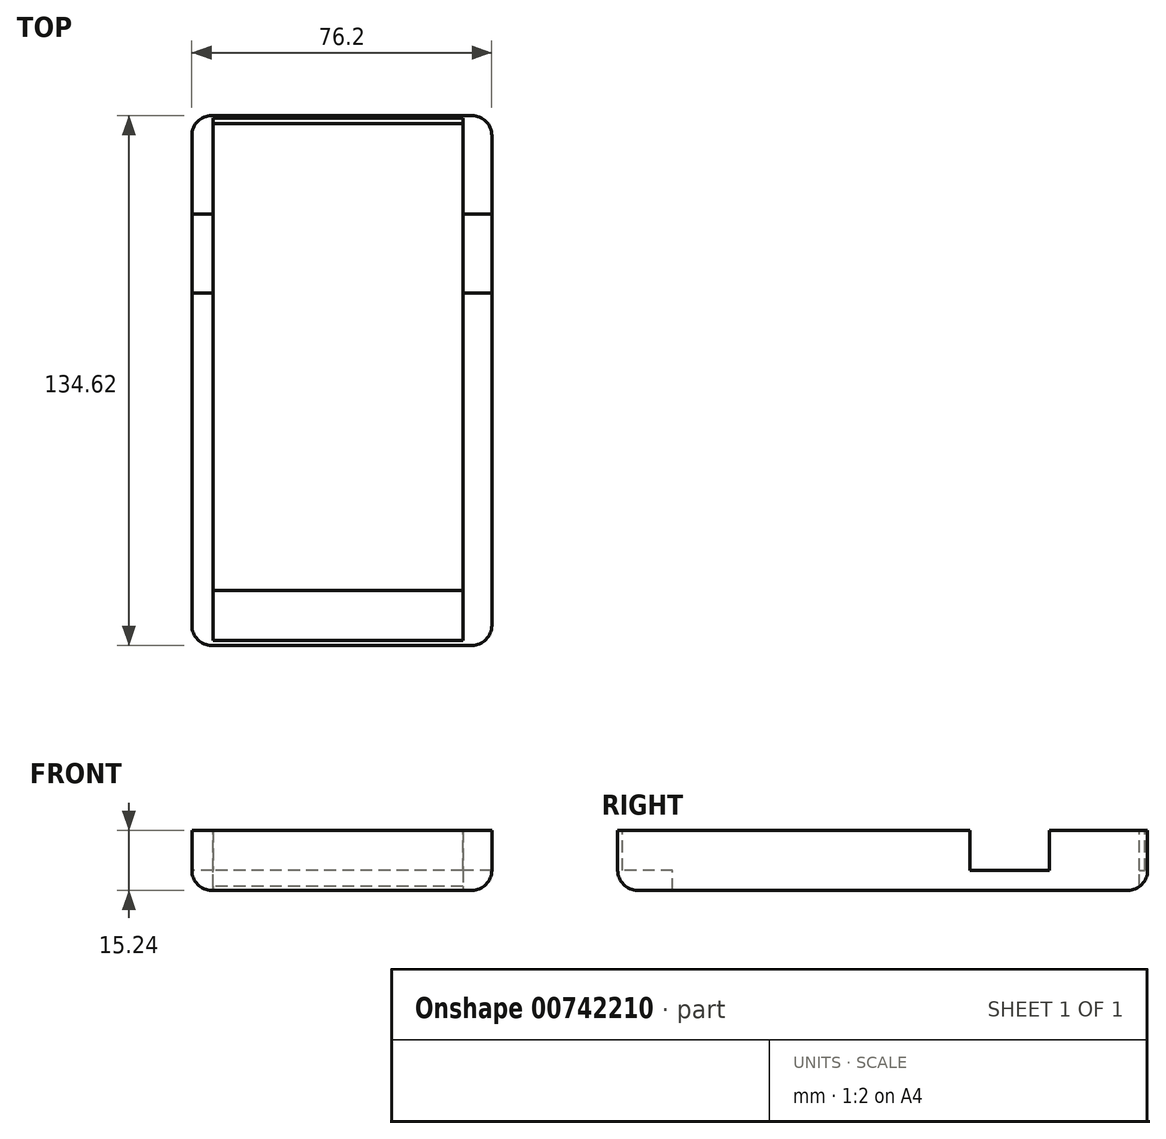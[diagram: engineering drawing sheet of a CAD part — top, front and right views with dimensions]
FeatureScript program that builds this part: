
annotation { "Feature Type Name" : "Feature", "Feature Type Description" : "" }
export const myFeature = defineFeature(function(context is Context, id is Id, definition is map)
    precondition{}
    {
        {
            var Q0;
            Q0=qCreatedBy(makeId("Top.planeOp"),FACE);
            var sketch = newSketch(context, id + "F0", { "sketchPlane" : qUnion([Q0])});
            skLineSegment(sketch, "E0.bottom", {"start": v(-32.63, 82.97) * mm, "end": v(43.57, 82.97) * mm});
            skLineSegment(sketch, "E0.top", {"start": v(-32.63, -51.65) * mm, "end": v(43.57, -51.65) * mm});
            skLineSegment(sketch, "E0.left", {"start": v(-32.63, 82.97) * mm, "end": v(-32.63, -51.65) * mm});
            skLineSegment(sketch, "E0.right", {"start": v(43.57, 82.97) * mm, "end": v(43.57, -51.65) * mm});
            skSolve(sketch);
        }
        {
            var Q0;
            Q0=makeQuery(id+"F0.imprint","IMPRINT",FACE,{"disambiguationData":[TD([[makeQuery(id+"F0.imprint","IMPRINT",EDGE,{"derivedFrom":sQuery(id+"F0.wireOp",EDGE,"E0.bottom")}),-1.0]])]});
            extrude(context, id + "F1", {"entities" : qUnion([Q0]), "depth" : 15.24 * mm, "offsetDistance" : 25.4 * mm});
        }
        {
            var Q0;
            Q0=makeQuery(id+"F0.imprint","IMPRINT",FACE,{"disambiguationData":[TD([[makeQuery(id+"F0.imprint","IMPRINT",EDGE,{"derivedFrom":sQuery(id+"F0.wireOp",EDGE,"E0.bottom")}),-1.0]])]});
            var sketch = newSketch(context, id + "F2", { "sketchPlane" : qUnion([Q0])});
            skLineSegment(sketch, "E1.bottom", {"start": v(-27.3, -37.69) * mm, "end": v(36.2, -37.69) * mm});
            skLineSegment(sketch, "E1.top", {"start": v(-27.3, 80.92) * mm, "end": v(36.2, 80.92) * mm});
            skLineSegment(sketch, "E1.left", {"start": v(-27.3, -37.69) * mm, "end": v(-27.3, 80.92) * mm});
            skLineSegment(sketch, "E1.right", {"start": v(36.2, -37.69) * mm, "end": v(36.2, 80.92) * mm});
            skLineSegment(sketch, "E2.bottom", {"start": v(36.2, 80.92) * mm, "end": v(-27.3, 80.92) * mm});
            skLineSegment(sketch, "E2.top", {"start": v(36.2, 81.81) * mm, "end": v(-27.3, 81.81) * mm});
            skLineSegment(sketch, "E2.left", {"start": v(36.2, 80.92) * mm, "end": v(36.2, 81.81) * mm});
            skLineSegment(sketch, "E2.right", {"start": v(-27.3, 80.92) * mm, "end": v(-27.3, 81.81) * mm});
            skSolve(sketch);
        }
        {
            var Q0;
            Q0=makeQuery(id+"F2.imprint","IMPRINT",FACE,{"disambiguationData":[TD([[makeQuery(id+"F2.imprint","IMPRINT",EDGE,{"derivedFrom":sQuery(id+"F2.wireOp",EDGE,"E1.bottom")}),1.0]])]});
            extrude(context, id + "F3", {"entities" : qUnion([Q0]), "operationType" : NewBodyOperationType.REMOVE, "endBound" : BoundingType.THROUGH_ALL, "depth" : 25.4 * mm, "offsetDistance" : 25.4 * mm});
        }
        {
            var Q0;
            Q0=makeQuery(id+"F1.opExtrude","CAP_FACE",FACE,{"disambiguationData":[OSD([sQuery(id+"F0.wireOp",EDGE,"E0.bottom"),sQuery(id+"F0.wireOp",EDGE,"E0.top"),sQuery(id+"F0.wireOp",EDGE,"E0.left"),sQuery(id+"F0.wireOp",EDGE,"E0.right")])],"isStart":false});
            var sketch = newSketch(context, id + "F4", { "sketchPlane" : qUnion([Q0])});
            skLineSegment(sketch, "E3.bottom", {"start": v(36.2, -37.69) * mm, "end": v(-27.3, -37.69) * mm});
            skLineSegment(sketch, "E3.top", {"start": v(36.2, -50.38) * mm, "end": v(-27.3, -50.38) * mm});
            skLineSegment(sketch, "E3.left", {"start": v(36.2, -37.69) * mm, "end": v(36.2, -50.38) * mm});
            skLineSegment(sketch, "E3.right", {"start": v(-27.3, -37.69) * mm, "end": v(-27.3, -50.38) * mm});
            skSolve(sketch);
        }
        {
            var Q0;
            Q0=makeQuery(id+"F4.imprint","IMPRINT",FACE,{"disambiguationData":[TD([[makeQuery(id+"F4.imprint","IMPRINT",EDGE,{"derivedFrom":sQuery(id+"F4.wireOp",EDGE,"E3.bottom")}),1.0]])]});
            extrude(context, id + "F5", {"entities" : qUnion([Q0]), "operationType" : NewBodyOperationType.REMOVE, "oppositeDirection" : true, "depth" : 10.16 * mm, "offsetDistance" : 25.4 * mm});
        }
        {
            var Q0;
            Q0=makeQuery(id+"F4.imprint","IMPRINT",FACE,{"disambiguationData":[TD([[makeQuery(id+"F4.imprint","IMPRINT",EDGE,{"derivedFrom":sQuery(id+"F4.wireOp",EDGE,"E3.top")}),1.0]])]});
            var sketch = newSketch(context, id + "F6", { "sketchPlane" : qUnion([Q0])});
            skLineSegment(sketch, "E4.bottom", {"start": v(36.2, 80.91) * mm, "end": v(-27.3, 80.91) * mm});
            skLineSegment(sketch, "E4.top", {"start": v(36.2, 82.33) * mm, "end": v(-27.3, 82.33) * mm});
            skLineSegment(sketch, "E4.left", {"start": v(36.2, 80.91) * mm, "end": v(36.2, 82.33) * mm});
            skLineSegment(sketch, "E4.right", {"start": v(-27.3, 80.91) * mm, "end": v(-27.3, 82.33) * mm});
            skSolve(sketch);
        }
        {
            var Q0;
            {var subQ1=sQuery(id+"F6.wireOp",EDGE,"E4.top");Q0=makeQuery(id+"F6.imprint","IMPRINT",FACE,{"disambiguationData":[TD([[makeQuery(id+"F6.imprint","IMPRINT",EDGE,{"derivedFrom":subQ1}),1.0]])]});}
            extrude(context, id + "F7", {"entities" : qUnion([Q0]), "operationType" : NewBodyOperationType.REMOVE, "oppositeDirection" : true, "depth" : 10.16 * mm, "offsetDistance" : 25.4 * mm});
        }
        {
            var Q0;
            Q0=makeQuery(id+"F1.opExtrude","CAP_EDGE",EDGE,{"disambiguationData":[OSD([sQuery(id+"F0.wireOp",EDGE,"E0.right")])],"isStart":true});
            var Q1;
            Q1=makeQuery(id+"F1.opExtrude","CAP_EDGE",EDGE,{"disambiguationData":[OSD([sQuery(id+"F0.wireOp",EDGE,"E0.bottom")])],"isStart":true});
            var Q2;
            Q2=makeQuery(id+"F1.opExtrude","CAP_EDGE",EDGE,{"disambiguationData":[OSD([sQuery(id+"F0.wireOp",EDGE,"E0.left")])],"isStart":true});
            var Q3;
            Q3=makeQuery(id+"F1.opExtrude","CAP_EDGE",EDGE,{"disambiguationData":[OSD([sQuery(id+"F0.wireOp",EDGE,"E0.top")])],"isStart":true});
            fillet(context, id + "F8", {"entities" : qUnion([Q0, Q1, Q2, Q3]), "radius" : 5.08 * mm, "tangentPropagation" : true, "allowEdgeOverflow" : false});
        }
        {
            var Q0;
            {var subQ0=sQuery(id+"F0.wireOp",EDGE,"E0.left");Q0=makeQuery(id+"F8.opFillet","BLEND_EDGE",EDGE,{"blendedFrom":[makeQuery(id+"F1.opExtrude","CAP_EDGE",EDGE,{"disambiguationData":[OSD([subQ0])],"isStart":true}),makeQuery(id+"F1.opExtrude","SWEPT_FACE",FACE,{"disambiguationData":[OSD([subQ0])]})],"blendedInto":[makeQuery(id+"F1.opExtrude","SWEPT_FACE",FACE,{"disambiguationData":[OSD([subQ0])]})]});}
            var Q1;
            Q1=makeQuery(id+"F8.opFillet","BLEND_EDGE",EDGE,{"blendedFrom":[makeQuery(id+"F1.opExtrude","CAP_EDGE",EDGE,{"disambiguationData":[OSD([sQuery(id+"F0.wireOp",EDGE,"E0.top")])],"isStart":true}),makeQuery(id+"F1.opExtrude","CAP_EDGE",EDGE,{"disambiguationData":[OSD([sQuery(id+"F0.wireOp",EDGE,"E0.left")])],"isStart":true})],"blendedInto":[]});
            var Q2;
            Q2=makeQuery(id+"F8.opFillet","BLEND_EDGE",EDGE,{"blendedFrom":[makeQuery(id+"F1.opExtrude","CAP_EDGE",EDGE,{"disambiguationData":[OSD([sQuery(id+"F0.wireOp",EDGE,"E0.bottom")])],"isStart":true}),makeQuery(id+"F1.opExtrude","CAP_EDGE",EDGE,{"disambiguationData":[OSD([sQuery(id+"F0.wireOp",EDGE,"E0.left")])],"isStart":true})],"blendedInto":[]});
            var Q3;
            Q3=makeQuery(id+"F8.opFillet","BLEND_EDGE",EDGE,{"blendedFrom":[makeQuery(id+"F1.opExtrude","CAP_EDGE",EDGE,{"disambiguationData":[OSD([sQuery(id+"F0.wireOp",EDGE,"E0.bottom")])],"isStart":true}),makeQuery(id+"F1.opExtrude","CAP_EDGE",EDGE,{"disambiguationData":[OSD([sQuery(id+"F0.wireOp",EDGE,"E0.right")])],"isStart":true})],"blendedInto":[]});
            var Q4;
            Q4=makeQuery(id+"F8.opFillet","BLEND_EDGE",EDGE,{"blendedFrom":[makeQuery(id+"F1.opExtrude","CAP_EDGE",EDGE,{"disambiguationData":[OSD([sQuery(id+"F0.wireOp",EDGE,"E0.top")])],"isStart":true}),makeQuery(id+"F1.opExtrude","CAP_EDGE",EDGE,{"disambiguationData":[OSD([sQuery(id+"F0.wireOp",EDGE,"E0.right")])],"isStart":true})],"blendedInto":[]});
            fillet(context, id + "F9", {"entities" : qUnion([Q0, Q1, Q2, Q3, Q4]), "radius" : 5.08 * mm, "tangentPropagation" : true, "allowEdgeOverflow" : false});
        }
        {
            var Q0;
            Q0=makeQuery(id+"F1.opExtrude","SWEPT_FACE",FACE,{"disambiguationData":[OSD([sQuery(id+"F0.wireOp",EDGE,"E0.left")])]});
            var sketch = newSketch(context, id + "F10", { "sketchPlane" : qUnion([Q0])});
            skLineSegment(sketch, "E5", {"start": v(-83.37, 10.16) * mm, "end": v(-57.97, 10.16) * mm});
            skPoint(sketch, "E5.startSnap0", {"position": v(-77.9, 10.16) * mm});
            skLineSegment(sketch, "E6", {"start": v(51.05, 10.16) * mm, "end": v(-37.85, 10.16) * mm});
            skPoint(sketch, "E6.startSnap0", {"position": v(46.57, 10.16) * mm});
            skLineSegment(sketch, "E7.bottom", {"start": v(-37.85, 15.24) * mm, "end": v(-57.97, 15.24) * mm});
            skLineSegment(sketch, "E7.top", {"start": v(-37.85, 5.08) * mm, "end": v(-57.97, 5.08) * mm});
            skLineSegment(sketch, "E7.left", {"start": v(-37.85, 15.24) * mm, "end": v(-37.85, 5.08) * mm});
            skLineSegment(sketch, "E7.right", {"start": v(-57.97, 15.24) * mm, "end": v(-57.97, 5.08) * mm});
            skSolve(sketch);
        }
        {
            var Q0;
            {var subQ5=sQuery(id+"F10.wireOp",EDGE,"E7.bottom");Q0=makeQuery(id+"F10.imprint","IMPRINT",FACE,{"disambiguationData":[TD([[makeQuery(id+"F10.imprint","IMPRINT",EDGE,{"derivedFrom":subQ5}),-1.0]])]});}
            extrude(context, id + "F11", {"entities" : qUnion([Q0]), "operationType" : NewBodyOperationType.REMOVE, "endBound" : BoundingType.THROUGH_ALL, "oppositeDirection" : true, "depth" : 25.4 * mm, "offsetDistance" : 25.4 * mm});
        }
    });
